# Revit family: Desk_Accessories-Teknion-BAPSE_Personal_Screen_Felt-R2018
name_source: partatom
category: Furniture
revit_build: Autodesk Revit 2018 (Build: 20190510_1515(x64)
units: mm (PartAtom-declared; Revit-internal decimal feet)

## family parameters
Always vertical = Yes
Cut with Voids When Loaded = No
OmniClass Number = 23.40.20.00
OmniClass Title = General Furniture and Specialties
Room Calculation Point = No
Shared = Yes
Work Plane-Based = Yes

## types (3) — shared parameters
Assembly Code = E2020200
Default Elevation = 48 "
Manufacturer = Teknion
Manufacturer Fax = 416.661.4586
Model = BAPSE181094
Part Number = BAPSE
Product Documentation Link = https://www.teknion.com
Product Line = Expansion Casegoods
Product Page URL = https://www.teknion.com
Series = Expansion Casegoods
Sustainability Data = https://www.teknion.com
URL = www.teknion.com
Unit Weight URL = http://www.teknion.com
Warranty = http://www.teknion.com

## per-type parameters (varying)
| type | Description | Worksurface Thickness |
| Mounted on a 1" Thick Worksurface | Personal Screen - Felt, 18" Width, 10" Height, 4" Depth, Mounted on a 1" Thick Worksurface | 1.016 " |
| Mounted on a 1 3/16" Thick Worksurface | Personal Screen - Felt, 18" Width, 10" Height, 4" Depth, Mounted on a 1 3/16" Thick Worksurface | 1.189 " |
| Mounted on a 1 9/16" Thick Worksurface | Personal Screen - Felt, 18" Width, 10" Height, 4" Depth, Mounted on a 1 9/16" Thick Worksurface | 1.555 " |

## geometry (parser evidence)
native form markers: Sweep x2
no freeform markers — native parametric forms only
